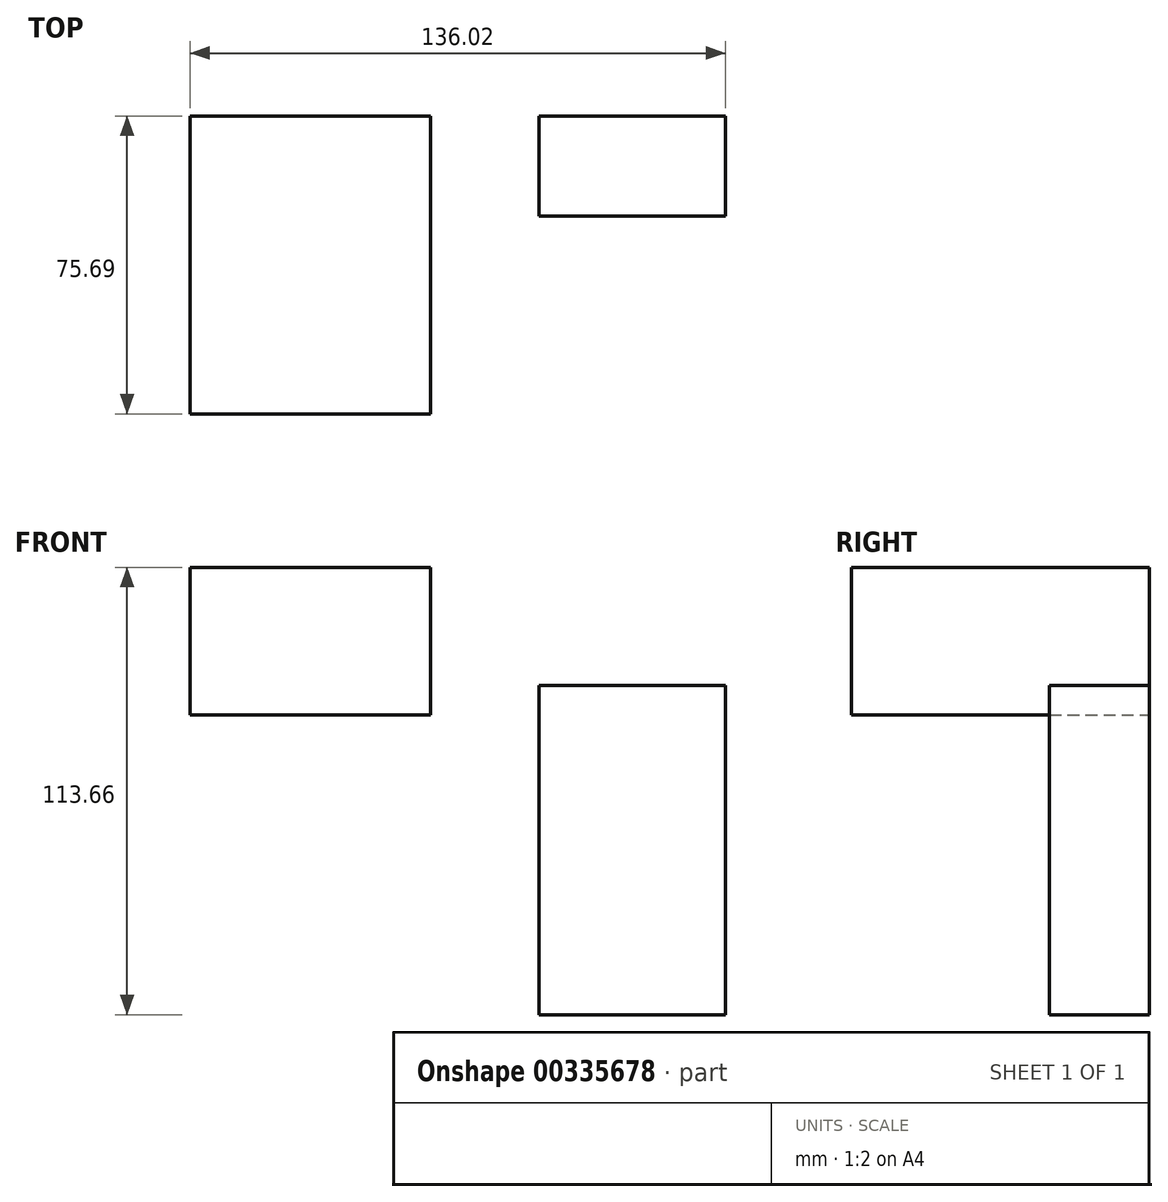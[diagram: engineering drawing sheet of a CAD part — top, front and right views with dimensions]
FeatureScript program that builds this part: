
annotation { "Feature Type Name" : "Feature", "Feature Type Description" : "" }
export const myFeature = defineFeature(function(context is Context, id is Id, definition is map)
    precondition{}
    {
        {
            var Q0;
            Q0=qCreatedBy(makeId("Front.planeOp"),FACE);
            var sketch = newSketch(context, id + "F0", { "sketchPlane" : qUnion([Q0])});
            skLineSegment(sketch, "E0", {"start": v(-68.64, -75.96) * mm, "end": v(-68.64, 102.3) * mm});
            skLineSegment(sketch, "E1", {"start": v(-68.64, 102.3) * mm, "end": v(8.33, 102.3) * mm});
            skLineSegment(sketch, "E2", {"start": v(8.33, 102.3) * mm, "end": v(8.33, -76.4) * mm});
            skLineSegment(sketch, "E3.bottom", {"start": v(27.52, -76.12) * mm, "end": v(74.95, -76.12) * mm});
            skLineSegment(sketch, "E3.top", {"start": v(27.52, 7.47) * mm, "end": v(74.95, 7.47) * mm});
            skLineSegment(sketch, "E3.left", {"start": v(27.52, -76.12) * mm, "end": v(27.52, 7.47) * mm});
            skLineSegment(sketch, "E3.right", {"start": v(74.95, -76.12) * mm, "end": v(74.95, 7.47) * mm});
            skSolve(sketch);
        }
        {
            var Q0;
            Q0=makeQuery(id+"F0.imprint","IMPRINT",FACE,{"disambiguationData":[TD([[makeQuery(id+"F0.imprint","IMPRINT",EDGE,{"derivedFrom":sQuery(id+"F0.wireOp",EDGE,"E3.bottom")}),1.0]])]});
            extrude(context, id + "F1", {"entities" : qUnion([Q0]), "depth" : 25.4 * mm});
        }
        {
            var Q0;
            Q0=qCreatedBy(makeId("Front.planeOp"),FACE);
            var sketch = newSketch(context, id + "F2", { "sketchPlane" : qUnion([Q0])});
            skLineSegment(sketch, "E4.bottom", {"start": v(0, 0) * mm, "end": v(-61.07, 0) * mm});
            skLineSegment(sketch, "E4.top", {"start": v(0, 37.54) * mm, "end": v(-61.07, 37.54) * mm});
            skLineSegment(sketch, "E4.left", {"start": v(0, 0) * mm, "end": v(0, 37.54) * mm});
            skLineSegment(sketch, "E4.right", {"start": v(-61.07, 0) * mm, "end": v(-61.07, 37.54) * mm});
            skSolve(sketch);
        }
        {
            var Q0;
            Q0 = qSketchRegion(id + "F2", true);
            extrude(context, id + "F3", {"entities" : qUnion([Q0]), "depth" : 75.7 * mm, "offsetDistance" : 25.4 * mm});
        }
    });
